# Revit family: Sink-Top_Mount-Kitchen-KOHLER-ELATE-K-98738T
name_source: partatom
category: Plumbing Fixtures
revit_build: Autodesk Revit 2017 (Build: 20160225_1515(x64)
units: mm (PartAtom-declared; Revit-internal decimal feet)

## family parameters
Cut with Voids When Loaded = No
Host = Face
OmniClass Number = 23.31.13.00
OmniClass Title = Sinks
Part Type = Normal
Room Calculation Point = No
Round Connector Dimension = Use Diameter
Shared = No

## types (3) — shared parameters
ADA Compliant = No
Assembly Code = D2010400
CW Connection = No
Cold Water Inlet = Cold Water Inlet
Date Modified = 11/02/2020
Default Elevation = 36"
Drain Included = Yes
HW Connection = No
Height = 8 1/8"
Hot Water Inlet = Hot Water Inlet
Length = 33 7/16"
Manufacturer = KOHLER Co.
Master Format 2014 = 22 41 16
Master Format 2014 Name = Residential Lavatories and Sinks
Material = Stainless Steel
Product Name = ELATE
URL = http://www.kohler.com.cn
Vent Connection = No
Waste Connection = Yes
Waste Water Outlet 1 = Waste Water Outlet 1
Waste Water Outlet 2 = Waste Water Outlet 2
WaterSense Certified = No
Width = 18 1/2"

## per-type parameters (varying)
| type | Description | Finish | Model | Type |
| 2FD, AKF- Pearl Silver | SR SINK,2FD, AKF | Kohler-Metal-AKF-Pearl_Silver | K-98738T-2FD-AKF | 1 |
| 2KD, KS- Pearl Silver | SR SINK,2KD, KS | Kohler-Metal-KS-Pearl_Silver | K-98738T-2KD-KS | 2 |
| 2KD, NA- Stainless Steel | SR SINK,2KD,NA | Kohler-Metal-NA-Stainless_Steel_Wire_Drawing | K-98738T-2KD-NA | 3 |

## geometry (parser evidence)
native form markers: Sweep x4
no freeform markers — native parametric forms only
